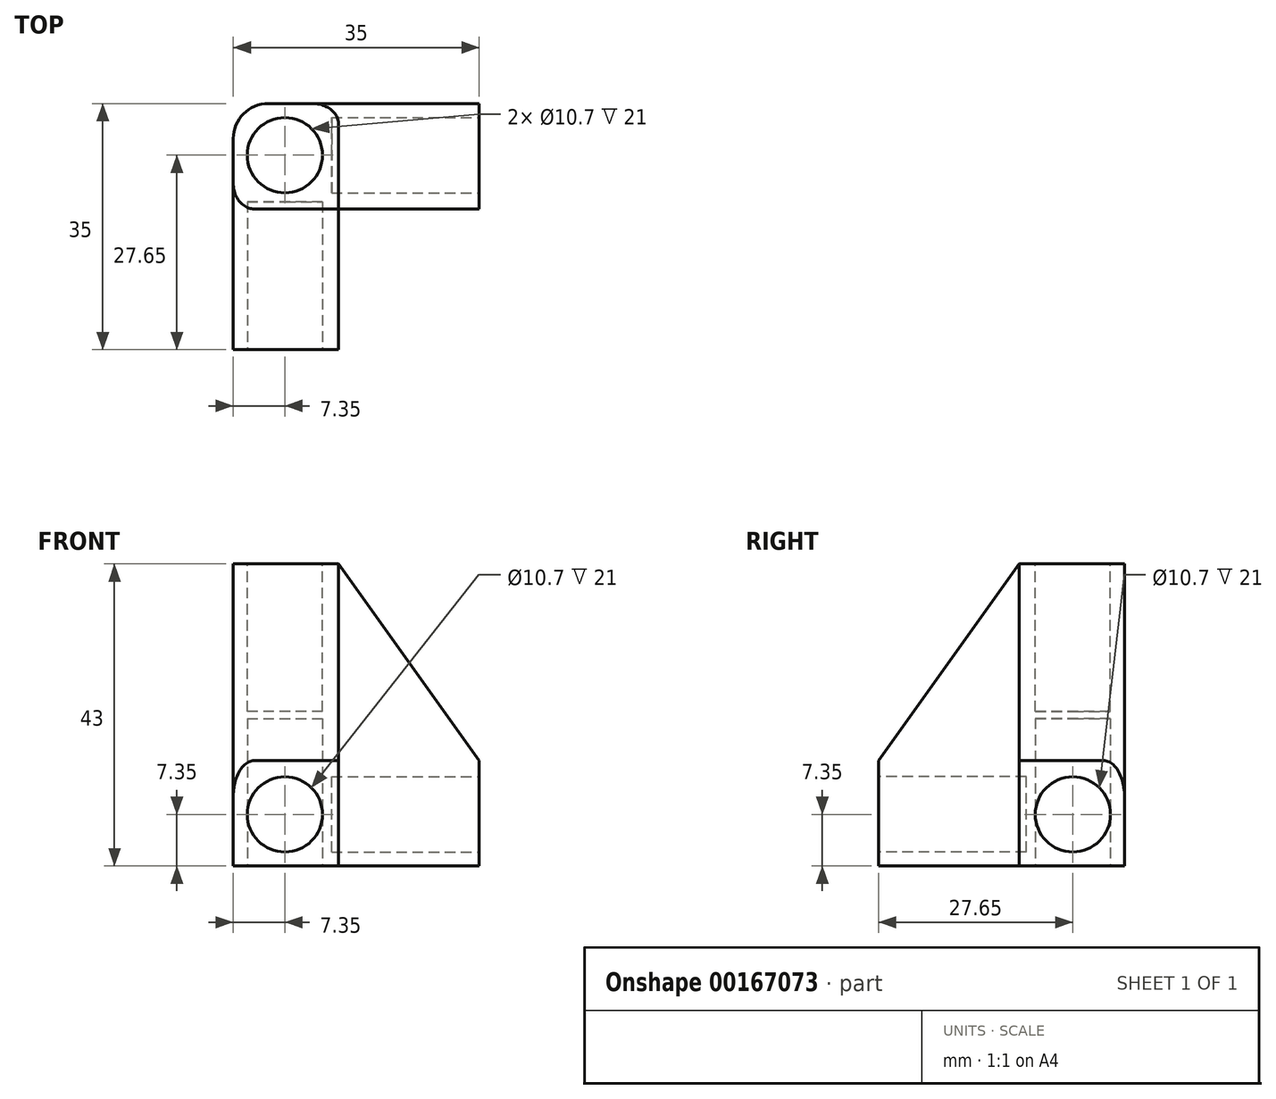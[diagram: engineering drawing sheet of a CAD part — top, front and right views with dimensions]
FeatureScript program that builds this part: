
annotation { "Feature Type Name" : "Feature", "Feature Type Description" : "" }
export const myFeature = defineFeature(function(context is Context, id is Id, definition is map)
    precondition{}
    {
        {
            var Q0;
            Q0=qCreatedBy(makeId("Top.planeOp"),FACE);
            var sketch = newSketch(context, id + "F0", { "sketchPlane" : qUnion([Q0])});
            skLineSegment(sketch, "E0.bottom", {"start": v(0, 0) * mm, "end": v(35, 0) * mm});
            skLineSegment(sketch, "E0.top", {"start": v(0, -35) * mm, "end": v(35, -35) * mm});
            skLineSegment(sketch, "E0.left", {"start": v(0, 0) * mm, "end": v(0, -35) * mm});
            skLineSegment(sketch, "E0.right", {"start": v(35, 0) * mm, "end": v(35, -35) * mm});
            skSolve(sketch);
        }
        {
            var Q0;
            Q0 = qSketchRegion(id + "F0", true);
            extrude(context, id + "F1", {"entities" : qUnion([Q0]), "depth" : 43 * mm});
        }
        {
            var Q0;
            Q0=makeQuery(id+"F1.opExtrude","SWEPT_FACE",FACE,{"disambiguationData":[OSD([sQuery(id+"F0.wireOp",EDGE,"E0.top")])]});
            var sketch = newSketch(context, id + "F2", { "sketchPlane" : qUnion([Q0])});
            skCircle(sketch, "E1", {"center": v(7.35, 7.35) * mm, "radius": 5.35 * mm});
            skSolve(sketch);
        }
        {
            var Q0;
            Q0 = qSketchRegion(id + "F2", true);
            extrude(context, id + "F3", {"entities" : qUnion([Q0]), "operationType" : NewBodyOperationType.REMOVE, "oppositeDirection" : true, "depth" : 21 * mm});
        }
        {
            var Q0;
            Q0=makeQuery(id+"F1.opExtrude","SWEPT_FACE",FACE,{"disambiguationData":[OSD([sQuery(id+"F0.wireOp",EDGE,"E0.right")])]});
            var sketch = newSketch(context, id + "F4", { "sketchPlane" : qUnion([Q0])});
            skCircle(sketch, "E2", {"center": v(-7.35, 7.35) * mm, "radius": 5.35 * mm});
            skSolve(sketch);
        }
        {
            var Q0;
            Q0 = qSketchRegion(id + "F4", true);
            extrude(context, id + "F5", {"entities" : qUnion([Q0]), "operationType" : NewBodyOperationType.REMOVE, "oppositeDirection" : true, "depth" : 21 * mm});
        }
        {
            var Q0;
            Q0=makeQuery(id+"F1.opExtrude","CAP_FACE",FACE,{"disambiguationData":[OSD([sQuery(id+"F0.wireOp",EDGE,"E0.bottom"),sQuery(id+"F0.wireOp",EDGE,"E0.top"),sQuery(id+"F0.wireOp",EDGE,"E0.left"),sQuery(id+"F0.wireOp",EDGE,"E0.right")])],"isStart":false});
            var sketch = newSketch(context, id + "F6", { "sketchPlane" : qUnion([Q0])});
            skCircle(sketch, "E3", {"center": v(7.35, -7.35) * mm, "radius": 5.35 * mm});
            skSolve(sketch);
        }
        {
            var Q0;
            Q0 = qSketchRegion(id + "F6", true);
            extrude(context, id + "F7", {"entities" : qUnion([Q0]), "operationType" : NewBodyOperationType.REMOVE, "oppositeDirection" : true, "depth" : 21 * mm});
        }
        {
            var Q0;
            Q0=makeQuery(id+"F1.opExtrude","CAP_FACE",FACE,{"disambiguationData":[OSD([sQuery(id+"F0.wireOp",EDGE,"E0.bottom"),sQuery(id+"F0.wireOp",EDGE,"E0.top"),sQuery(id+"F0.wireOp",EDGE,"E0.left"),sQuery(id+"F0.wireOp",EDGE,"E0.right")])],"isStart":false});
            var sketch = newSketch(context, id + "F8", { "sketchPlane" : qUnion([Q0])});
            skLineSegment(sketch, "E4.bottom", {"start": v(35, -35) * mm, "end": v(15, -35) * mm});
            skLineSegment(sketch, "E4.top", {"start": v(35, -15) * mm, "end": v(15, -15) * mm});
            skLineSegment(sketch, "E4.left", {"start": v(35, -35) * mm, "end": v(35, -15) * mm});
            skLineSegment(sketch, "E4.right", {"start": v(15, -35) * mm, "end": v(15, -15) * mm});
            skSolve(sketch);
        }
        {
            var Q0;
            Q0=makeQuery(id+"F8.imprint","IMPRINT",FACE,{"disambiguationData":[TD([[makeQuery(id+"F8.imprint","IMPRINT",EDGE,{"derivedFrom":sQuery(id+"F8.wireOp",EDGE,"E4.bottom")}),1.0]])]});
            extrude(context, id + "F9", {"entities" : qUnion([Q0]), "operationType" : NewBodyOperationType.REMOVE, "endBound" : BoundingType.THROUGH_ALL, "oppositeDirection" : true, "depth" : 25 * mm});
        }
        {
            var Q0;
            Q0=makeQuery(id+"F1.opExtrude","CAP_FACE",FACE,{"disambiguationData":[OSD([sQuery(id+"F0.wireOp",EDGE,"E0.bottom"),sQuery(id+"F0.wireOp",EDGE,"E0.top"),sQuery(id+"F0.wireOp",EDGE,"E0.left"),sQuery(id+"F0.wireOp",EDGE,"E0.right")])],"isStart":true});
            var sketch = newSketch(context, id + "F10", { "sketchPlane" : qUnion([Q0])});
            skCircle(sketch, "E5", {"center": v(7.35, 7.35) * mm, "radius": 5.35 * mm});
            skSolve(sketch);
        }
        {
            var Q0;
            Q0 = qSketchRegion(id + "F10", true);
            extrude(context, id + "F11", {"entities" : qUnion([Q0]), "operationType" : NewBodyOperationType.REMOVE, "oppositeDirection" : true, "depth" : 21 * mm});
        }
        {
            var Q0;
            Q0=makeQuery(id+"F1.opExtrude","CAP_EDGE",EDGE,{"disambiguationData":[OSD([sQuery(id+"F0.wireOp",EDGE,"E0.right")])],"isStart":false});
            var Q1;
            Q1=makeQuery(id+"F1.opExtrude","CAP_EDGE",EDGE,{"disambiguationData":[OSD([sQuery(id+"F0.wireOp",EDGE,"E0.top")])],"isStart":false});
            chamfer(context, id + "F12", {"entities" : qUnion([Q0, Q1]), "chamferType" : ChamferType.TWO_OFFSETS, "width1" : 28 * mm, "oppositeDirection" : false, "width2" : 20 * mm, "tangentPropagation" : true});
        }
        {
            var Q0;
            Q0=makeQuery(id+"F1.opExtrude","SWEPT_EDGE",EDGE,{"disambiguationData":[OSD([sQuery(id+"F0.wireOp",EDGE,"E0.bottom"),sQuery(id+"F0.wireOp",EDGE,"E0.left")])]});
            fillet(context, id + "F13", {"entities" : qUnion([Q0]), "radius" : 5 * mm, "tangentPropagation" : true, "allowEdgeOverflow" : false});
        }
        {
            var Q0;
            Q0=makeQuery(id+"F12.opChamfer","BLEND_EDGE",EDGE,{"blendedFrom":[makeQuery(id+"F1.opExtrude","CAP_EDGE",EDGE,{"disambiguationData":[OSD([sQuery(id+"F0.wireOp",EDGE,"E0.top")])],"isStart":false}),makeQuery(id+"F1.opExtrude","SWEPT_FACE",FACE,{"disambiguationData":[OSD([sQuery(id+"F0.wireOp",EDGE,"E0.left")])]})],"blendedInto":[makeQuery(id+"F1.opExtrude","SWEPT_FACE",FACE,{"disambiguationData":[OSD([sQuery(id+"F0.wireOp",EDGE,"E0.left")])]})]});
            var Q1;
            Q1=makeQuery(id+"F12.opChamfer","BLEND_EDGE",EDGE,{"blendedFrom":[makeQuery(id+"F1.opExtrude","CAP_EDGE",EDGE,{"disambiguationData":[OSD([sQuery(id+"F0.wireOp",EDGE,"E0.right")])],"isStart":false}),makeQuery(id+"F1.opExtrude","SWEPT_FACE",FACE,{"disambiguationData":[OSD([sQuery(id+"F0.wireOp",EDGE,"E0.bottom")])]})],"blendedInto":[makeQuery(id+"F1.opExtrude","SWEPT_FACE",FACE,{"disambiguationData":[OSD([sQuery(id+"F0.wireOp",EDGE,"E0.bottom")])]})]});
            fillet(context, id + "F14", {"entities" : qUnion([Q0, Q1]), "radius" : 3 * mm, "tangentPropagation" : true, "allowEdgeOverflow" : false});
        }
    });
